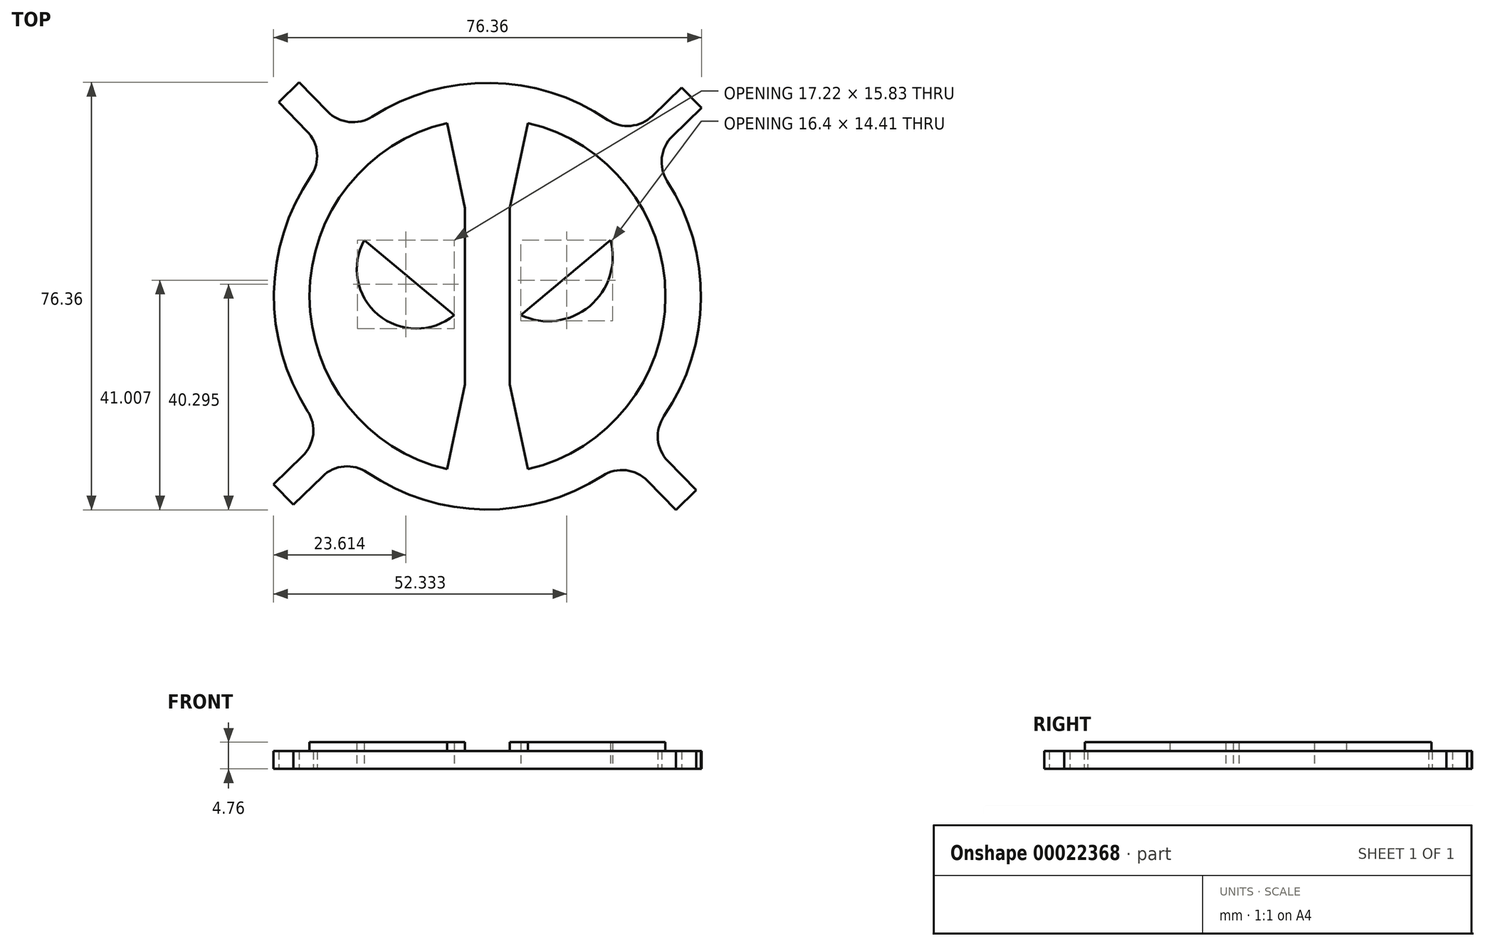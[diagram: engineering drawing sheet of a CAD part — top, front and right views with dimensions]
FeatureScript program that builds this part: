
annotation { "Feature Type Name" : "Feature", "Feature Type Description" : "" }
export const myFeature = defineFeature(function(context is Context, id is Id, definition is map)
    precondition{}
    {
        {
            var Q0;
            Q0=qCreatedBy(makeId("Top.planeOp"),FACE);
            var sketch = newSketch(context, id + "F0", { "sketchPlane" : qUnion([Q0])});
            skArc(sketch, "E0", {"start": v(-7.23, 30.92) * mm, "mid": v(-31.75, 0) * mm, "end": v(-7.23, -30.92) * mm});
            skArc(sketch, "E1", {"start": v(-31.5, 21.44) * mm, "mid": v(-38.1, 0.52) * mm, "end": v(-32.07, -20.57) * mm});
            skLineSegment(sketch, "E2", {"start": v(-4, 15.75) * mm, "end": v(-4, -15.75) * mm});
            skLineSegment(sketch, "E3", {"start": v(4, 15.75) * mm, "end": v(4, -15.75) * mm});
            skLineSegment(sketch, "E4", {"start": v(-4, 0) * mm, "end": v(-4, 15.75) * mm});
            skLineSegment(sketch, "E5", {"start": v(-4, 0) * mm, "end": v(-4, -15.75) * mm});
            skLineSegment(sketch, "E6", {"start": v(4, 0) * mm, "end": v(4, -15.75) * mm});
            skLineSegment(sketch, "E7", {"start": v(-4, 15.75) * mm, "end": v(-7.23, 30.92) * mm});
            skLineSegment(sketch, "E8", {"start": v(4, 15.75) * mm, "end": v(7.23, 30.92) * mm});
            skLineSegment(sketch, "E9", {"start": v(-4, -15.75) * mm, "end": v(-7.23, -30.92) * mm});
            skLineSegment(sketch, "E10", {"start": v(4, -15.75) * mm, "end": v(7.23, -30.92) * mm});
            skLineSegment(sketch, "E11", {"start": v(-5.95, -3.4) * mm, "end": v(-15.98, 5) * mm});
            skLineSegment(sketch, "E12", {"start": v(5.95, -3.4) * mm, "end": v(15.98, 5) * mm});
            skArc(sketch, "E13", {"start": v(-21.97, 10.03) * mm, "mid": v(-19.52, -3.31) * mm, "end": v(-5.95, -3.4) * mm});
            skPoint(sketch, "E14.orphan", {"position": v(0, 31.5) * mm});
            skPoint(sketch, "E15.orphan", {"position": v(4, 31.5) * mm});
            skPoint(sketch, "E16.orphan", {"position": v(-4, 31.5) * mm});
            skPoint(sketch, "E17.orphan", {"position": v(-4, -31.5) * mm});
            skPoint(sketch, "E18.end.orphan", {"position": v(4, -31.5) * mm});
            skPoint(sketch, "E19.end.orphan", {"position": v(0, -31.5) * mm});
            skPoint(sketch, "E20.orphan", {"position": v(-4, -5.04) * mm});
            skPoint(sketch, "E21.orphan", {"position": v(4, -5.04) * mm});
            skArc(sketch, "E22.trimOffspring", {"start": v(7.23, -30.92) * mm, "mid": v(31.75, 0) * mm, "end": v(7.23, 30.92) * mm});
            skPoint(sketch, "E23.end.orphan", {"position": v(27.95, 15.05) * mm});
            skPoint(sketch, "E24.end.orphan", {"position": v(-27.95, 15.05) * mm});
            skPoint(sketch, "E25.end.orphan", {"position": v(15.98, 5) * mm});
            skLineSegment(sketch, "E26", {"start": v(-21.97, 10.03) * mm, "end": v(-15.98, 5) * mm});
            skLineSegment(sketch, "E27", {"start": v(4, -15.75) * mm, "end": v(4, 15.75) * mm});
            skLineSegment(sketch, "E28", {"start": v(-37.25, 34.64) * mm, "end": v(-32.2, 29.44) * mm});
            skLineSegment(sketch, "E29", {"start": v(-33.6, 38.18) * mm, "end": v(-28.55, 32.99) * mm});
            skLineSegment(sketch, "E30", {"start": v(34.64, 37.25) * mm, "end": v(29.44, 32.2) * mm});
            skLineSegment(sketch, "E31", {"start": v(38.18, 33.6) * mm, "end": v(32.99, 28.55) * mm});
            skLineSegment(sketch, "E32", {"start": v(-38.18, -33.6) * mm, "end": v(-32.99, -28.55) * mm});
            skLineSegment(sketch, "E33", {"start": v(37.25, -34.64) * mm, "end": v(32.2, -29.44) * mm});
            skLineSegment(sketch, "E34", {"start": v(-38.18, -33.6) * mm, "end": v(-34.64, -37.25) * mm});
            skLineSegment(sketch, "E35", {"start": v(-29.44, -32.2) * mm, "end": v(-34.64, -37.25) * mm});
            skLineSegment(sketch, "E36", {"start": v(28.55, -32.99) * mm, "end": v(33.6, -38.18) * mm});
            skLineSegment(sketch, "E37", {"start": v(37.25, -34.64) * mm, "end": v(33.6, -38.18) * mm});
            skLineSegment(sketch, "E38", {"start": v(-37.25, 34.64) * mm, "end": v(-33.6, 38.18) * mm});
            skLineSegment(sketch, "E39", {"start": v(34.64, 37.25) * mm, "end": v(38.18, 33.6) * mm});
            skLineSegment(sketch, "E40", {"start": v(-4.08, 28.63) * mm, "end": v(1.26, 28.63) * mm});
            skArc(sketch, "E41", {"start": v(-3.76, 24.78) * mm, "mid": v(-2.46, 26.49) * mm, "end": v(-2.3, 28.63) * mm});
            skLineSegment(sketch, "E42", {"start": v(-2.46, 26.49) * mm, "end": v(-0.66, 26.49) * mm});
            skArc(sketch, "E43", {"start": v(-3.52, 21.8) * mm, "mid": v(-1.47, 23.77) * mm, "end": v(-0.66, 26.49) * mm});
            skLineSegment(sketch, "E44", {"start": v(-3.1, 25.4) * mm, "end": v(-2.06, 24.78) * mm});
            skLineSegment(sketch, "E45", {"start": v(-4.08, 28.63) * mm, "end": v(3.54, 28.63) * mm});
            skLineSegment(sketch, "E46", {"start": v(1.26, 28.63) * mm, "end": v(1.26, 23.5) * mm});
            skLineSegment(sketch, "E47", {"start": v(2.53, 22.23) * mm, "end": v(4.24, 22.23) * mm});
            skLineSegment(sketch, "E48", {"start": v(4.24, 22.23) * mm, "end": v(4.24, 23.75) * mm});
            skLineSegment(sketch, "E49", {"start": v(1.26, 25.1) * mm, "end": v(2.9, 27.16) * mm});
            skPoint(sketch, "E50.visualSharp", {"position": v(1.26, 22.23) * mm});
            skArc(sketch, "E50.filletArc", {"start": v(1.26, 23.5) * mm, "mid": v(1.63, 22.6) * mm, "end": v(2.53, 22.23) * mm});
            skPoint(sketch, "E51.trimOffspring.end.orphan", {"position": v(0, 31.75) * mm});
            skPoint(sketch, "E52.start.orphan", {"position": v(0, -31.75) * mm});
            skArc(sketch, "E53", {"start": v(5.95, -3.4) * mm, "mid": v(18.23, -1.78) * mm, "end": v(21.97, 10.03) * mm});
            skArc(sketch, "E54.trimOffspring", {"start": v(21.44, 31.5) * mm, "mid": v(0.52, 38.1) * mm, "end": v(-20.57, 32.07) * mm});
            skArc(sketch, "E55.trimOffspring", {"start": v(31.5, -21.44) * mm, "mid": v(38.1, -0.52) * mm, "end": v(32.07, 20.57) * mm});
            skArc(sketch, "E56.trimOffspring", {"start": v(-21.44, -31.5) * mm, "mid": v(-0.52, -38.1) * mm, "end": v(20.57, -32.07) * mm});
            skPoint(sketch, "E57.visualSharp", {"position": v(-24.69, 29.02) * mm});
            skArc(sketch, "E57.filletArc", {"start": v(-28.55, 32.99) * mm, "mid": v(-24.72, 31.1) * mm, "end": v(-20.57, 32.07) * mm});
            skPoint(sketch, "E58.visualSharp", {"position": v(-28.33, 25.48) * mm});
            skArc(sketch, "E58.filletArc", {"start": v(-31.5, 21.44) * mm, "mid": v(-30.42, 25.57) * mm, "end": v(-32.2, 29.44) * mm});
            skPoint(sketch, "E59.visualSharp", {"position": v(-29.02, -24.69) * mm});
            skArc(sketch, "E59.filletArc", {"start": v(-32.99, -28.55) * mm, "mid": v(-31.1, -24.72) * mm, "end": v(-32.07, -20.57) * mm});
            skPoint(sketch, "E60.visualSharp", {"position": v(-25.48, -28.33) * mm});
            skArc(sketch, "E60.filletArc", {"start": v(-21.44, -31.5) * mm, "mid": v(-25.57, -30.42) * mm, "end": v(-29.44, -32.2) * mm});
            skPoint(sketch, "E61.visualSharp", {"position": v(24.69, -29.02) * mm});
            skArc(sketch, "E61.filletArc", {"start": v(28.55, -32.99) * mm, "mid": v(24.72, -31.1) * mm, "end": v(20.57, -32.07) * mm});
            skPoint(sketch, "E62.visualSharp", {"position": v(28.33, -25.48) * mm});
            skArc(sketch, "E62.filletArc", {"start": v(31.5, -21.44) * mm, "mid": v(30.42, -25.57) * mm, "end": v(32.2, -29.44) * mm});
            skPoint(sketch, "E63.visualSharp", {"position": v(29.02, 24.69) * mm});
            skArc(sketch, "E63.filletArc", {"start": v(32.99, 28.55) * mm, "mid": v(31.1, 24.72) * mm, "end": v(32.07, 20.57) * mm});
            skPoint(sketch, "E64.visualSharp", {"position": v(25.48, 28.33) * mm});
            skArc(sketch, "E64.filletArc", {"start": v(21.44, 31.5) * mm, "mid": v(25.57, 30.42) * mm, "end": v(29.44, 32.2) * mm});
            skLineSegment(sketch, "E65", {"start": v(15.98, 5) * mm, "end": v(21.97, 10.03) * mm});
            skSolve(sketch);
        }
        {
            var Q0;
            Q0=makeQuery(id+"F0.imprint","IMPRINT",FACE,{"disambiguationData":[TD([[makeQuery(id+"F0.imprint","IMPRINT",EDGE,{"derivedFrom":sQuery(id+"F0.wireOp",EDGE,"E0")}),-1.0]])]});
            extrude(context, id + "F1", {"entities" : qUnion([Q0]), "depth" : 3.17 * mm});
        }
        {
            var Q0;
            {var subQ2=sQuery(id+"F0.wireOp",EDGE,"E8");Q0=makeQuery(id+"F0.imprint","IMPRINT",FACE,{"disambiguationData":[TD([[makeQuery(id+"F0.imprint","IMPRINT",EDGE,{"derivedFrom":subQ2}),-1.0]])]});}
            var Q1;
            Q1=makeQuery(id+"F0.imprint","IMPRINT",FACE,{"disambiguationData":[TD([[makeQuery(id+"F0.imprint","IMPRINT",EDGE,{"derivedFrom":sQuery(id+"F0.wireOp",EDGE,"E0")}),1.0]])]});
            extrude(context, id + "F2", {"entities" : qUnion([Q0, Q1]), "operationType" : NewBodyOperationType.ADD, "depth" : 4.76 * mm});
        }
        {
            var Q0;
            {var subQ1=sQuery(id+"F0.wireOp",EDGE,"E28");Q0=makeQuery(id+"F0.imprint","IMPRINT",FACE,{"disambiguationData":[TD([[makeQuery(id+"F0.imprint","IMPRINT",EDGE,{"derivedFrom":subQ1}),1.0]])]});}
            var Q1;
            {var subQ1=sQuery(id+"F0.wireOp",EDGE,"E32");Q1=makeQuery(id+"F0.imprint","IMPRINT",FACE,{"disambiguationData":[TD([[makeQuery(id+"F0.imprint","IMPRINT",EDGE,{"derivedFrom":subQ1}),-1.0]])]});}
            var Q2;
            {var subQ1=sQuery(id+"F0.wireOp",EDGE,"E33");Q2=makeQuery(id+"F0.imprint","IMPRINT",FACE,{"disambiguationData":[TD([[makeQuery(id+"F0.imprint","IMPRINT",EDGE,{"derivedFrom":subQ1}),1.0]])]});}
            var Q3;
            {var subQ1=sQuery(id+"F0.wireOp",EDGE,"E30");Q3=makeQuery(id+"F0.imprint","IMPRINT",FACE,{"disambiguationData":[TD([[makeQuery(id+"F0.imprint","IMPRINT",EDGE,{"derivedFrom":subQ1}),1.0]])]});}
            extrude(context, id + "F3", {"entities" : qUnion([Q0, Q1, Q2, Q3]), "operationType" : NewBodyOperationType.ADD, "depth" : 3.17 * mm});
        }
    });
